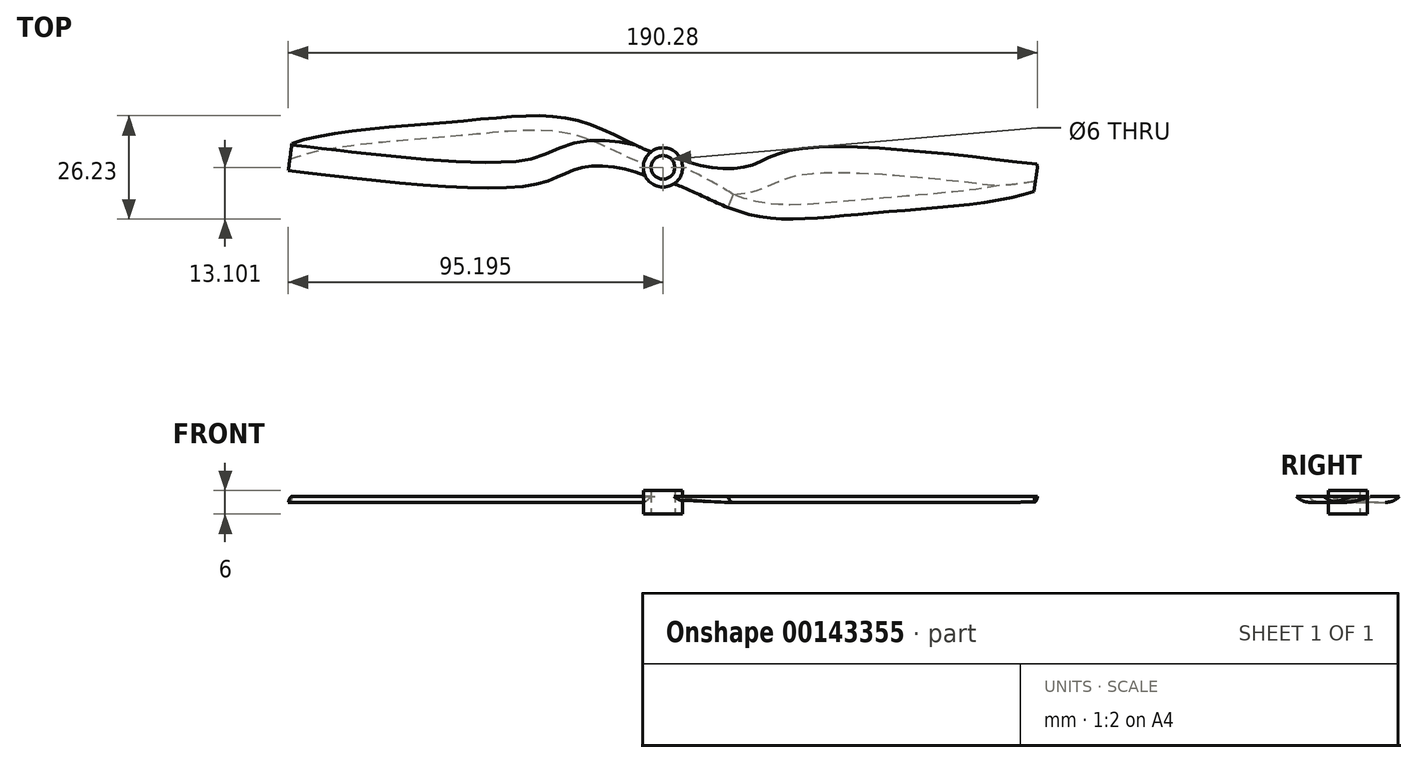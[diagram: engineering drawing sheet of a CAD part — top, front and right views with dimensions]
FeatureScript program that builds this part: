
annotation { "Feature Type Name" : "Feature", "Feature Type Description" : "" }
export const myFeature = defineFeature(function(context is Context, id is Id, definition is map)
    precondition{}
    {
        {
            var Q0;
            Q0=qCreatedBy(makeId("Top.planeOp"),FACE);
            var sketch = newSketch(context, id + "F0", { "sketchPlane" : qUnion([Q0])});
            skCircle(sketch, "E0", {"center": v(-19.1, -1.25) * mm, "radius": 5 * mm});
            skCircle(sketch, "E1", {"center": v(-19.1, -1.25) * mm, "radius": 3 * mm});
            skFitSpline(sketch, "E2", {"points": [v(-22.06, 2.78) * mm, v(-40.42, 10.54) * mm, v(-70.17, 10.54) * mm, v(-113.36, 4.85) * mm], "startDerivative": vector(-51.08, 15.58) * mm, "endDerivative": vector(-70.31, -25.59) * mm});
            skFitSpline(sketch, "E3", {"points": [v(-23.66, -3.3) * mm, v(-39.49, -1.25) * mm, v(-52.32, -5.74) * mm, v(-114.3, -2.04) * mm], "startDerivative": vector(-50.64, 23.12) * mm, "endDerivative": vector(-111.74, 12.85) * mm});
            skLineSegment(sketch, "E4", {"start": v(-113.36, 4.85) * mm, "end": v(-114.3, -2.04) * mm});
            skLineSegment(sketch, "E5.MirrorCS", {"start": v(75.87, -0.43) * mm, "end": v(76.1, -2.04) * mm});
            skFitSpline(sketch, "E6.MirrorCS", {"points": [v(-16.35, -5.42) * mm, v(2.21, -13.04) * mm, v(31.96, -13.04) * mm, v(75.15, -7.35) * mm], "startDerivative": vector(51.08, -15.58) * mm, "endDerivative": vector(70.31, 25.59) * mm});
            skFitSpline(sketch, "E7.MirrorCS", {"points": [v(-14.6, 0.91) * mm, v(1.28, -1.25) * mm, v(14.11, 3.24) * mm, v(76.1, -0.46) * mm], "startDerivative": vector(50.64, -23.12) * mm, "endDerivative": vector(111.74, -12.85) * mm});
            skPoint(sketch, "E8.MirrorCS.end.orphan", {"position": v(75.15, 4.85) * mm});
            skPoint(sketch, "E8.MirrorCS.start.orphan", {"position": v(-16.15, 2.78) * mm});
            skLineSegment(sketch, "E9", {"start": v(76.1, -0.46) * mm, "end": v(75.15, -7.35) * mm});
            skSolve(sketch);
        }
        {
            var Q0;
            Q0=makeQuery(id+"F0.imprint","IMPRINT",FACE,{"disambiguationData":[TD([[makeQuery(id+"F0.imprint","IMPRINT",EDGE,{"derivedFrom":sQuery(id+"F0.wireOp",EDGE,"E1")}),-1.0]])]});
            extrude(context, id + "F1", {"entities" : qUnion([Q0]), "depth" : 3 * mm, "hasSecondDirection" : true, "secondDirectionOppositeDirection" : true, "secondDirectionDepth" : 3 * mm});
        }
        {
            var Q0;
            {var subQ0=sQuery(id+"F0.wireOp",EDGE,"E2");Q0=makeQuery(id+"F0.imprint","IMPRINT",FACE,{"disambiguationData":[TD([[makeQuery(id+"F0.imprint","IMPRINT",EDGE,{"derivedFrom":subQ0}),1.0]])]});}
            var Q1;
            {var subQ5=sQuery(id+"F0.wireOp",EDGE,"E6.MirrorCS");Q1=makeQuery(id+"F0.imprint","IMPRINT",FACE,{"disambiguationData":[TD([[makeQuery(id+"F0.imprint","IMPRINT",EDGE,{"derivedFrom":subQ5}),1.0]])]});}
            extrude(context, id + "F2", {"entities" : qUnion([Q0, Q1]), "operationType" : NewBodyOperationType.ADD, "depth" : 1.5 * mm});
        }
        {
            var Q0;
            Q0=makeQuery(id+"F2.opExtrude","CAP_EDGE",EDGE,{"disambiguationData":[OSD([sQuery(id+"F0.wireOp",EDGE,"E3")])],"isStart":false});
            var Q1;
            Q1=makeQuery(id+"F2.opExtrude","CAP_EDGE",EDGE,{"disambiguationData":[OSD([sQuery(id+"F0.wireOp",EDGE,"E7.MirrorCS")])],"isStart":true});
            fillet(context, id + "F3", {"entities" : qUnion([Q0, Q1]), "radius" : 15 * mm, "tangentPropagation" : true, "allowEdgeOverflow" : false});
        }
        {
            var Q0;
            Q0=makeQuery(id+"F2.opExtrude","CAP_EDGE",EDGE,{"disambiguationData":[OSD([sQuery(id+"F0.wireOp",EDGE,"E2")])],"isStart":true});
            var Q1;
            Q1=makeQuery(id+"F2.opExtrude","CAP_EDGE",EDGE,{"disambiguationData":[OSD([sQuery(id+"F0.wireOp",EDGE,"E6.MirrorCS")])],"isStart":true});
            fillet(context, id + "F4", {"entities" : qUnion([Q0, Q1]), "radius" : 5 * mm, "tangentPropagation" : true, "allowEdgeOverflow" : false});
        }
    });
